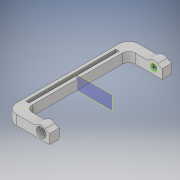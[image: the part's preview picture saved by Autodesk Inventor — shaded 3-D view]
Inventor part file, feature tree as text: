
AUTODESK INVENTOR PART (.ipt)
format: ipt  version: 2018 (Build 220112000, 112)  size: 233,984 bytes
history: native  units: in
note: dims shown in document units (in); Inventor stores cm internally (conversion verified against a paired STEP export)
features: sketch x17, extrude x10, fillet x6, hole x2, plane x1, mirror x1
ambient origin geometry x8: Origin, YZ Plane, XZ Plane, XY Plane, X Axis, Y Axis, Z Axis, Center Point
bodies: Solid1 (feature_tree)
feature tree (37):
  extrude  "Extrusion1"  Depth=0.375in
  sketch  "Sketch2"  dims[d3=0.375in d4=0.5in d5=0.375in d6=0.0in]
  extrude  "Extrusion2"  Depth=0.375in
  fillet  "Fillet1"  Radius=0.375in
  extrude  "Extrusion3"  Depth=0.375in
  extrude  "Extrusion4"  Depth=0.25in
  plane  "Work Plane1"
  mirror  "Mirror1"
  fillet  "Fillet2"  Radius=0.24in
  extrude  "Extrusion5"  Depth=0.375in
  sketch  "Sketch6"  dims[d17=1.0in d18=0.0in d19=0.24in d20=0.0in]
  extrude  "Extrusion6"  Depth=0.24in TaperAngle=0.0deg
  extrude  "Extrusion7"  Depth=0.375in
  fillet  "Fillet3"  Radius=0.25in
  fillet  "Fillet4"  Radius=0.375in
  fillet  "Fillet5"  Radius=0.25in
  fillet  "Fillet6"  Radius=0.125in
  sketch  "Sketch9"  dims[d30=0.125in d31=0.125in]
  extrude  "Extrusion8"  Depth=0.035in
  sketch  "Sketch11"  dims[d35=0.2in]
  sketch  "Sketch12"  dims[d36=0.2in d37=0.75in d38=0.375in d39=0.25in d40=0.5635in d41=0.35in d42=0.0in]
  hole  "Hole1"  [1 undecoded]
  hole  "Hole2"  [1 undecoded]
  sketch  "Sketch14"  dims[d51=3.5in d52=0.375in d53=0.0in]
  extrude  "Extrusion9"  Depth=0.125in
  extrude  "Extrusion10"  Depth=0.375in TaperAngle=0.0deg
  sketch  "Sketch17"
  sketch  "Sketch1"  dims[d0=1.3in d1=0.375in]
  sketch  "Sketch3"  dims[d7=0.375in d8=0.0in d9=0.375in]
  sketch  "Sketch4"  dims[d10=0.24in d11=0.0in d12=0.25in d13=0.24in d14=0.0in]
  sketch  "Sketch5"  dims[d15=2.0in d16=0.375in]
  sketch  "Sketch7"  dims[d21=0.375in d22=0.0in d23=0.375in d24=0.25in d25=0.375in d26=0.25in d27=0.125in]
  sketch  "Sketch8"  dims[d28=0.035in d29=0.035in]
  sketch  "Sketch10"  dims[d32=4.375in d33=0.0in d34=0.2in]
  sketch  "Sketch13"  dims[d43=0.2in d44=0.75in d45=0.375in d46=0.25in d47=0.5635in d48=0.35in d49=0.0in d50=0.125in]
  sketch  "Sketch15"  dims[d54=1.0in d55=0.0in]
  sketch  "Sketch16"
note: 2 required parameter values undecoded (feature->parameter linkage not recoverable at this tier; creation-order binding heuristic only, values carry confidence <= 0.55)
